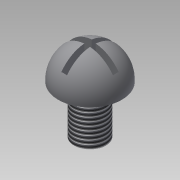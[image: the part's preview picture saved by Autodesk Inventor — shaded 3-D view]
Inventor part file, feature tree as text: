
AUTODESK INVENTOR PART (.ipt)
format: ipt  version: 2015 (Build 190159000, 159)  size: 210,944 bytes
history: native  units: mm
features: sketch x6, extrude x4, revolve x2, projected_geometry x2, thread x1
ambient origin geometry x8: Origin, YZ Plane, XZ Plane, XY Plane, X Axis, Y Axis, Z Axis, Center Point
bodies: Solid1 (feature_tree)
feature tree (15):
  extrude  "Extrusion1"  Depth=3.0mm TaperAngle=0.0deg
  extrude  "Extrusion2"  Depth=0.1mm TaperAngle=0.0deg
  revolve  "Revolution1"  Angle=90.0deg
  extrude  "Extrusion3"  Depth=10.0mm TaperAngle=360.0deg
  revolve  "Revolution2"  [1 undecoded]
  extrude  "Extrusion4"  [1 undecoded]
  thread  "Thread1"  [1 undecoded]
  sketch  "Sketch1"  dims[d0=2.0mm d1=3.0mm d2=0.0mm]
  sketch  "Sketch2"  dims[d3=4.0mm d4=0.1mm d5=0.0mm]
  sketch  "Sketch3"  dims[d6=40.0mm d8=360.0deg d10=90.0deg]
  sketch  "Sketch4"  dims[d11=10.0mm d12=0.0mm d14=40.0mm d15=360.0deg]
  projected_geometry  "Projected Loop2"
  sketch  "Sketch5"  dims[d16=90.0deg d17=10.0mm d18=0.0mm]
  sketch  "Sketch6"  dims[d19=10.0mm d20=0.0mm]
  projected_geometry  "Projected Loop4"
note: 3 required parameter values undecoded (feature->parameter linkage not recoverable at this tier; creation-order binding heuristic only, values carry confidence <= 0.55)